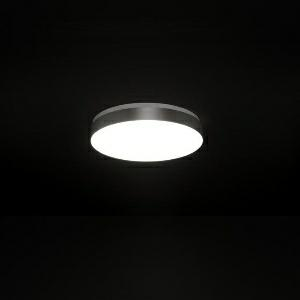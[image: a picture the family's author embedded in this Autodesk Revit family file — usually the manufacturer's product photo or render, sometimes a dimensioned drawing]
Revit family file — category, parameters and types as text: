
# Revit family: spectral_norea_norea-ra_416_4300_840_mps_e365
name_source: partatom
category: Lighting Fixtures
revit_build: Autodesk Revit 2016 (Build: 20150220_1215(x64)
units: mm (PartAtom-declared; Revit-internal decimal feet)

## family parameters
Cut with Voids When Loaded = No
Host = Face
Light Source = No
Part Type = Normal
Room Calculation Point = No
Round Connector Dimension = Use Diameter
Shared = No

## types (1)
- SPECTRAL NOREA (1 x )
    Apparent Load = 0 VA
    Approval mark = CE
    CIE Flux Codes = 73 93 98 100 62
    Control Gear = Electronic transformer
    Default Elevation = 1800 mm
    Description = SPT0000084
NOREA surface-mounted luminaire

Design:
Round luminaire element with a microprism panel in a natural anodised aluminium profile frame surround. The frame is fixed at the powder-coated metal body by a bayonet fixture with spring clip. The metal body accommodates the electrical components and electronic ballast. The LED module is formed as a round LED flat board and can be removed for mounting or exchange using a keyhole screw connection. Plug-in electrical connection of the LED flat board. Luminaire with heat-resistant wiring. Variant suitable for office use with a microprism panel MPS. The LED points are visible as circles on the microprism panel. Suitable for ceiling or wall mounting. Also in a dimmable version. Protection rating IP20, safety class I

Colour:
Housing – similar to RAL 9016 White silk matt;
Frame – natural anodised
    Height = 80 mm  [stored 0.262467 ft]
    Lamp = 1 x
    Lamp count = 1
    Length = 416 mm
    Luminous efficacy = 0 lm/W
    Manufacturer = Ridi
    ModVariant = No
    Model = NOREA-RA 416/4300/840 MPS
    Mounting Place = Ceiling
    Mounting Type = Surface mounted
    Number of Poles = 1
    OnlyDefault = Yes
    Power Factor = 1
    Product Name = SPECTRAL NOREA
    Product group = Ceiling mounted luminaire
    ProductGroupID = 3
    Protection Class = Protection class
    Protection Degree = IP 20
    RlxData = <blob elided: 30125 chars, md5=fff2a649>
    Socket = socket
    Standby Power = 0 W
    System Light Flux = 0 lm
    System Power = 0 W
    Type Image = rundmittel01_-_kopie.jpg
    URL = http://reluxnet.relux.com
    VarID = 1
    Voltage = 0 V
    Weight = 0.00 kg
    Width = 0 mm  [stored 0 ft]

note: [stored X ft] marks values corroborated as IEEE doubles in the binary element streams (Revit-internal decimal feet)

## geometry (parser evidence)
native form markers: Sweep x12
no freeform markers — native parametric forms only
